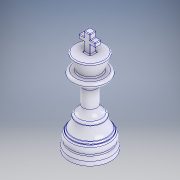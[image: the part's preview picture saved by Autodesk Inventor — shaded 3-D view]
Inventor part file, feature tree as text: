
AUTODESK INVENTOR PART (.ipt)
format: ipt  version: 2018 (Build 220112000, 112)  size: 370,176 bytes
history: native  units: in
note: dims shown in document units (in); Inventor stores cm internally (conversion verified against a paired STEP export)
features: fillet x14, extrude x10, sketch x10, chamfer x3, draft x1
ambient origin geometry x8: Origin, YZ Plane, XZ Plane, XY Plane, X Axis, Y Axis, Z Axis, Center Point
bodies: Solid1 (feature_tree)
feature tree (38):
  extrude  "Extrusion1"  Depth=0.2in TaperAngle=0.0deg
  fillet  "Fillet1"  Radius=0.1in
  extrude  "Extrusion2"  Depth=0.1in
  fillet  "Fillet2"  Radius=0.025in
  fillet  "Fillet3"  Radius=0.096in
  chamfer  "Chamfer1"  Distance=0.0625in
  extrude  "Extrusion3"  Depth=0.125in
  chamfer  "Chamfer2"  Distance=0.2835in
  fillet  "Fillet4"  Radius=0.375in
  fillet  "Fillet5"  Radius=0.0625in
  fillet  "Fillet6"  Radius=0.33in
  extrude  "Extrusion4"  Depth=0.1875in
  fillet  "Fillet7"  Radius=0.125in
  fillet  "Fillet8"  Radius=0.1875in
  extrude  "Extrusion5"  Depth=0.475in
  fillet  "Fillet9"  Radius=0.375in
  extrude  "Extrusion6"  Depth=0.148in
  fillet  "Fillet10"  Radius=0.4375in
  fillet  "Fillet11"  Radius=0.125in
  extrude  "Extrusion7"  Depth=0.125in TaperAngle=0.0deg
  draft  "FaceDraft1"
  extrude  "Extrusion8"  Depth=0.0225in
  extrude  "Extrusion9"  Depth=0.0225in
  extrude  "Extrusion10"  Depth=0.0225in
  fillet  "Fillet12"  Radius=0.015in
  fillet  "Fillet13"  [1 undecoded]
  fillet  "Fillet14"  [1 undecoded]
  chamfer  "Chamfer3"  [1 undecoded]
  sketch  "Sketch1"  dims[d0=1.0in d1=0.2in d2=0.0in d3=0.1in]
  sketch  "Sketch2"  dims[d4=0.2in d5=0.0in d6=0.1in d7=0.025in]
  sketch  "Sketch3"  dims[d8=0.0625in d9=0.125in d10=0.3917in d11=0.096in d12=0.0in d13=0.0625in d14=0.125in d15=0.3779in]
  sketch  "Sketch4"  dims[d16=0.025in d17=0.125in]
  sketch  "Sketch5"  dims[d18=0.125in d19=0.2835in d20=0.0in d21=0.375in d22=0.0625in d23=0.33in]
  sketch  "Sketch6"  dims[d24=0.75in d25=0.0in d26=0.1875in d27=0.125in d28=0.0in d29=0.1875in]
  sketch  "Sketch7"  dims[d30=0.0625in d31=0.475in d32=0.375in d33=0.0in]
  sketch  "Sketch8"  dims[d34=-0.1374in d35=0.148in d36=0.4375in d37=0.0in d38=0.125in]
  sketch  "Sketch9"  dims[d39=0.1in d40=0.125in d41=0.0in]
  sketch  "Sketch10"  dims[d42=0.125in d43=0.0in d44=0.0225in d45=0.0225in d46=0.0225in d47=0.015in d48=0.125in d49=45.0deg]
note: 3 required parameter values undecoded (feature->parameter linkage not recoverable at this tier; creation-order binding heuristic only, values carry confidence <= 0.55)
